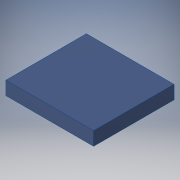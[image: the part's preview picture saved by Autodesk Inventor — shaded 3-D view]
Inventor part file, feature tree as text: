
AUTODESK INVENTOR PART (.ipt)
format: ipt  version: 2018 (Build 220112000, 112)  size: 104,448 bytes
history: native  units: in
note: dims shown in document units (in); Inventor stores cm internally (conversion verified against a paired STEP export)
features: extrude x1, sketch x1
ambient origin geometry x8: Origin, YZ Plane, XZ Plane, XY Plane, X Axis, Y Axis, Z Axis, Center Point
bodies: Solid1 (feature_tree)
feature tree (2):
  extrude  "Extrusion1"  Depth=0.7008in
  sketch  "Sketch1"  dims[d0=0.7638in d1=0.7008in d2=0.1181in d3=0.0in]
